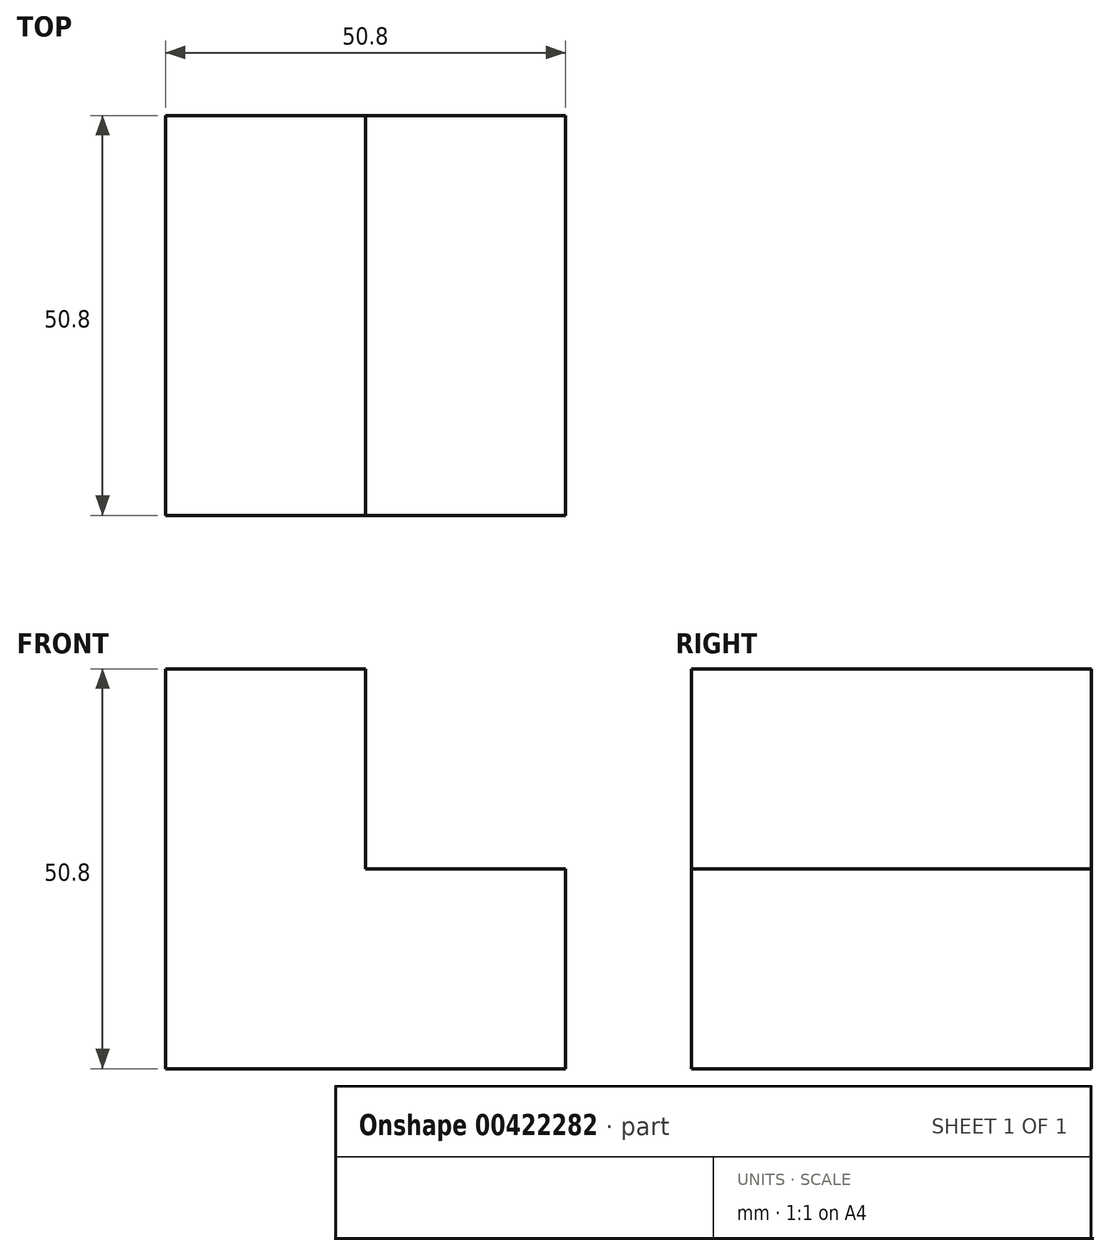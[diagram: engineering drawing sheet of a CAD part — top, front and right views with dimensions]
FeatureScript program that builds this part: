
annotation { "Feature Type Name" : "Feature", "Feature Type Description" : "" }
export const myFeature = defineFeature(function(context is Context, id is Id, definition is map)
    precondition{}
    {
        {
            var Q0;
            Q0=qCreatedBy(makeId("Front.planeOp"),FACE);
            var sketch = newSketch(context, id + "F0", { "sketchPlane" : qUnion([Q0])});
            skLineSegment(sketch, "E0", {"start": v(-60.7, 50.8) * mm, "end": v(-60.7, 0) * mm});
            skLineSegment(sketch, "E1", {"start": v(-60.7, 0) * mm, "end": v(-9.9, 0) * mm});
            skLineSegment(sketch, "E2", {"start": v(-9.9, 0) * mm, "end": v(-9.9, 25.4) * mm});
            skLineSegment(sketch, "E3", {"start": v(-9.9, 25.4) * mm, "end": v(-35.3, 25.4) * mm});
            skLineSegment(sketch, "E4", {"start": v(-35.3, 25.4) * mm, "end": v(-35.3, 50.8) * mm});
            skLineSegment(sketch, "E5", {"start": v(-35.3, 50.8) * mm, "end": v(-60.7, 50.8) * mm});
            skSolve(sketch);
        }
        {
            var Q0;
            Q0 = qSketchRegion(id + "F0", true);
            extrude(context, id + "F1", {"entities" : qUnion([Q0]), "depth" : 50.8 * mm});
        }
    });
